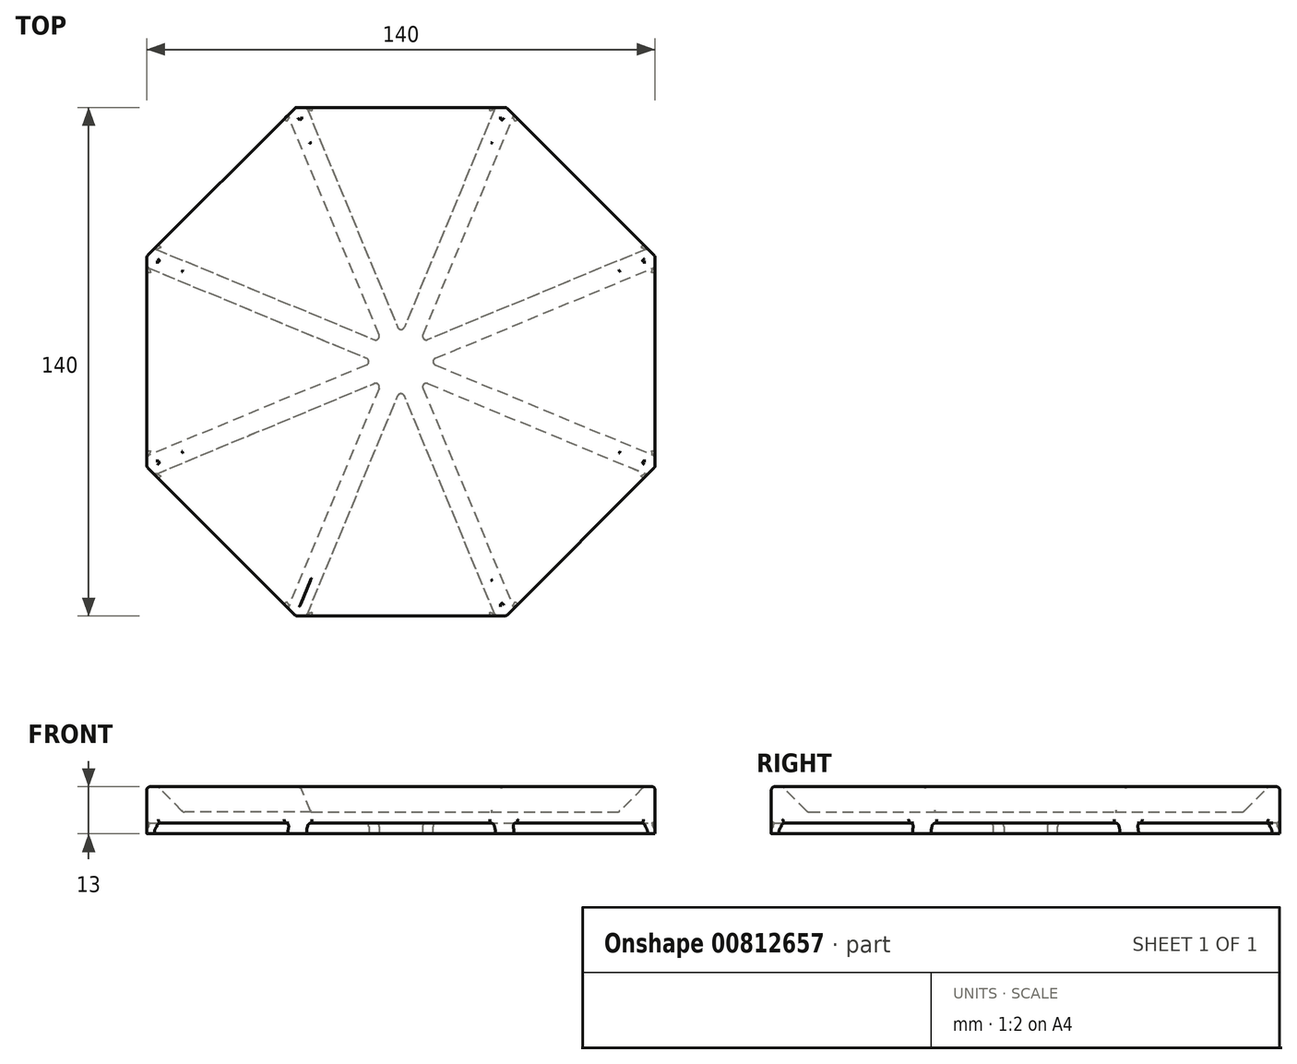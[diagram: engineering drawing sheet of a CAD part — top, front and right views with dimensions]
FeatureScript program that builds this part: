
annotation { "Feature Type Name" : "Feature", "Feature Type Description" : "" }
export const myFeature = defineFeature(function(context is Context, id is Id, definition is map)
    precondition{}
    {
        {
            var Q0;
            Q0=qCreatedBy(makeId("Top.planeOp"),FACE);
            var sketch = newSketch(context, id + "F0", { "sketchPlane" : qUnion([Q0])});
            skCircle(sketch, "E0.cCircle", {"center": v(0, 0) * mm, "radius": 70 * mm, "construction": true});
            skLineSegment(sketch, "E0.0", {"start": v(29, -70) * mm, "end": v(-29, -70) * mm});
            skLineSegment(sketch, "E0.1", {"start": v(-29, -70) * mm, "end": v(-70, -29) * mm});
            skLineSegment(sketch, "E0.2", {"start": v(-70, -29) * mm, "end": v(-70, 29) * mm});
            skLineSegment(sketch, "E0.3", {"start": v(-70, 29) * mm, "end": v(-29, 70) * mm});
            skLineSegment(sketch, "E0.4", {"start": v(-29, 70) * mm, "end": v(29, 70) * mm});
            skLineSegment(sketch, "E0.5", {"start": v(29, 70) * mm, "end": v(70, 29) * mm});
            skLineSegment(sketch, "E0.6", {"start": v(70, 29) * mm, "end": v(70, -29) * mm});
            skLineSegment(sketch, "E0.7", {"start": v(70, -29) * mm, "end": v(29, -70) * mm});
            skPoint(sketch, "E0.0.midPoint", {"position": v(0, -70) * mm});
            skSolve(sketch);
        }
        {
            var Q0;
            Q0 = qSketchRegion(id + "F0", true);
            extrude(context, id + "F1", {"entities" : qUnion([Q0]), "depth" : 10 * mm, "offsetDistance" : 25 * mm});
        }
        {
            var Q0;
            Q0=makeQuery(id+"F1.opExtrude","CAP_FACE",FACE,{"disambiguationData":[OSD([sQuery(id+"F0.wireOp",EDGE,"E0.0"),sQuery(id+"F0.wireOp",EDGE,"E0.1"),sQuery(id+"F0.wireOp",EDGE,"E0.2"),sQuery(id+"F0.wireOp",EDGE,"E0.3"),sQuery(id+"F0.wireOp",EDGE,"E0.4"),sQuery(id+"F0.wireOp",EDGE,"E0.5"),sQuery(id+"F0.wireOp",EDGE,"E0.6"),sQuery(id+"F0.wireOp",EDGE,"E0.7")])],"isStart":false});
            shell(context, id + "F2", {"entities" : qUnion([Q0]), "thickness" : 3 * mm});
        }
        {
            var Q0;
            Q0=makeQuery(id+"F2.opShell","OFFSET_FACE",FACE,{"disambiguationData":[OSD([sQuery(id+"F0.wireOp",EDGE,"E0.0"),sQuery(id+"F0.wireOp",EDGE,"E0.1"),sQuery(id+"F0.wireOp",EDGE,"E0.2"),sQuery(id+"F0.wireOp",EDGE,"E0.3"),sQuery(id+"F0.wireOp",EDGE,"E0.4"),sQuery(id+"F0.wireOp",EDGE,"E0.5"),sQuery(id+"F0.wireOp",EDGE,"E0.6"),sQuery(id+"F0.wireOp",EDGE,"E0.7")])]});
            chamfer(context, id + "F3", {"entities" : qUnion([Q0]), "width" : 7 * mm, "tangentPropagation" : true});
        }
        {
            var Q0;
            Q0=makeQuery(id+"F1.opExtrude","CAP_FACE",FACE,{"disambiguationData":[OSD([sQuery(id+"F0.wireOp",EDGE,"E0.0"),sQuery(id+"F0.wireOp",EDGE,"E0.1"),sQuery(id+"F0.wireOp",EDGE,"E0.2"),sQuery(id+"F0.wireOp",EDGE,"E0.3"),sQuery(id+"F0.wireOp",EDGE,"E0.4"),sQuery(id+"F0.wireOp",EDGE,"E0.5"),sQuery(id+"F0.wireOp",EDGE,"E0.6"),sQuery(id+"F0.wireOp",EDGE,"E0.7")])],"isStart":true});
            var sketch = newSketch(context, id + "F4", { "sketchPlane" : qUnion([Q0])});
            skLineSegment(sketch, "E1", {"start": v(-26, 70) * mm, "end": v(0, 7.24) * mm});
            skLineSegment(sketch, "E2", {"start": v(26, -70) * mm, "end": v(0, -7.24) * mm});
            skLineSegment(sketch, "E3", {"start": v(26, 70) * mm, "end": v(0, 7.24) * mm});
            skLineSegment(sketch, "E4", {"start": v(-26, -70) * mm, "end": v(0, -7.24) * mm});
            skLineSegment(sketch, "E5", {"start": v(-67.88, 31.12) * mm, "end": v(-5.12, 5.12) * mm});
            skLineSegment(sketch, "E6", {"start": v(67.88, -31.12) * mm, "end": v(5.12, -5.12) * mm});
            skLineSegment(sketch, "E7", {"start": v(-70, -26) * mm, "end": v(-7.24, 0) * mm});
            skLineSegment(sketch, "E8", {"start": v(-67.88, -31.12) * mm, "end": v(-5.12, -5.12) * mm});
            skLineSegment(sketch, "E9.trimOffspring", {"start": v(5.12, 5.12) * mm, "end": v(67.88, 31.12) * mm});
            skLineSegment(sketch, "E10.trimOffspring", {"start": v(5.12, 5.12) * mm, "end": v(31.12, 67.88) * mm});
            skLineSegment(sketch, "E11.trimOffspring", {"start": v(7.24, 0) * mm, "end": v(70, -26) * mm});
            skLineSegment(sketch, "E12.trimOffspring", {"start": v(7.24, 0) * mm, "end": v(70, 26) * mm});
            skLineSegment(sketch, "E13.trimOffspring", {"start": v(5.12, -5.12) * mm, "end": v(31.12, -67.88) * mm});
            skLineSegment(sketch, "E14.trimOffspring", {"start": v(-5.12, -5.12) * mm, "end": v(-31.12, -67.88) * mm});
            skLineSegment(sketch, "E15.trimOffspring", {"start": v(-7.24, 0) * mm, "end": v(-70, 26) * mm});
            skLineSegment(sketch, "E16.trimOffspring", {"start": v(-5.12, 5.12) * mm, "end": v(-31.12, 67.88) * mm});
            skSolve(sketch);
        }
        {
            var Q0;
            {var subQ8=sQuery(id+"F4.wireOp",EDGE,"E1");Q0=makeQuery(id+"F4.imprint","IMPRINT",FACE,{"disambiguationData":[TD([[makeQuery(id+"F4.imprint","IMPRINT",EDGE,{"derivedFrom":subQ8}),-1.0]])]});}
            extrude(context, id + "F5", {"entities" : qUnion([Q0]), "operationType" : NewBodyOperationType.ADD, "depth" : 3 * mm, "offsetDistance" : 25 * mm});
        }
        {
            var Q0;
            {var subQ0=sQuery(id+"F0.wireOp",EDGE,"E0.7");var subQ1=sQuery(id+"F0.wireOp",EDGE,"E0.0");var subQ5=sQuery(id+"F0.wireOp",EDGE,"E0.1");Q0=makeQuery(id+"F5.boolean.opBoolean","SPLIT",FACE,{"disambiguationData":[TD([makeQuery(id+"F1.opExtrude","SWEPT_FACE",FACE,{"disambiguationData":[OSD([subQ1])]})])],"derivedFrom":makeQuery(id+"F1.opExtrude","CAP_FACE",FACE,{"disambiguationData":[OSD([subQ1,subQ5,sQuery(id+"F0.wireOp",EDGE,"E0.2"),sQuery(id+"F0.wireOp",EDGE,"E0.3"),sQuery(id+"F0.wireOp",EDGE,"E0.4"),sQuery(id+"F0.wireOp",EDGE,"E0.5"),sQuery(id+"F0.wireOp",EDGE,"E0.6"),subQ0])],"isStart":true})});}
            var Q1;
            {var subQ0=sQuery(id+"F0.wireOp",EDGE,"E0.7");var subQ2=sQuery(id+"F0.wireOp",EDGE,"E0.0");var subQ5=sQuery(id+"F0.wireOp",EDGE,"E0.6");Q1=makeQuery(id+"F5.boolean.opBoolean","SPLIT",FACE,{"disambiguationData":[TD([makeQuery(id+"F1.opExtrude","SWEPT_FACE",FACE,{"disambiguationData":[OSD([subQ0])]})])],"derivedFrom":makeQuery(id+"F1.opExtrude","CAP_FACE",FACE,{"disambiguationData":[OSD([subQ2,sQuery(id+"F0.wireOp",EDGE,"E0.1"),sQuery(id+"F0.wireOp",EDGE,"E0.2"),sQuery(id+"F0.wireOp",EDGE,"E0.3"),sQuery(id+"F0.wireOp",EDGE,"E0.4"),sQuery(id+"F0.wireOp",EDGE,"E0.5"),subQ5,subQ0])],"isStart":true})});}
            var Q2;
            {var subQ0=sQuery(id+"F0.wireOp",EDGE,"E0.6");var subQ2=sQuery(id+"F0.wireOp",EDGE,"E0.5");var subQ5=sQuery(id+"F0.wireOp",EDGE,"E0.7");Q2=makeQuery(id+"F5.boolean.opBoolean","SPLIT",FACE,{"disambiguationData":[TD([makeQuery(id+"F1.opExtrude","SWEPT_FACE",FACE,{"disambiguationData":[OSD([subQ0])]})])],"derivedFrom":makeQuery(id+"F1.opExtrude","CAP_FACE",FACE,{"disambiguationData":[OSD([sQuery(id+"F0.wireOp",EDGE,"E0.0"),sQuery(id+"F0.wireOp",EDGE,"E0.1"),sQuery(id+"F0.wireOp",EDGE,"E0.2"),sQuery(id+"F0.wireOp",EDGE,"E0.3"),sQuery(id+"F0.wireOp",EDGE,"E0.4"),subQ2,subQ0,subQ5])],"isStart":true})});}
            var Q3;
            {var subQ0=sQuery(id+"F0.wireOp",EDGE,"E0.5");var subQ2=sQuery(id+"F0.wireOp",EDGE,"E0.4");var subQ5=sQuery(id+"F0.wireOp",EDGE,"E0.6");Q3=makeQuery(id+"F5.boolean.opBoolean","SPLIT",FACE,{"disambiguationData":[TD([makeQuery(id+"F1.opExtrude","SWEPT_FACE",FACE,{"disambiguationData":[OSD([subQ0])]})])],"derivedFrom":makeQuery(id+"F1.opExtrude","CAP_FACE",FACE,{"disambiguationData":[OSD([sQuery(id+"F0.wireOp",EDGE,"E0.0"),sQuery(id+"F0.wireOp",EDGE,"E0.1"),sQuery(id+"F0.wireOp",EDGE,"E0.2"),sQuery(id+"F0.wireOp",EDGE,"E0.3"),subQ2,subQ0,subQ5,sQuery(id+"F0.wireOp",EDGE,"E0.7")])],"isStart":true})});}
            var Q4;
            {var subQ1=sQuery(id+"F0.wireOp",EDGE,"E0.5");var subQ2=sQuery(id+"F0.wireOp",EDGE,"E0.4");var subQ5=sQuery(id+"F0.wireOp",EDGE,"E0.3");Q4=makeQuery(id+"F5.boolean.opBoolean","SPLIT",FACE,{"disambiguationData":[TD([makeQuery(id+"F1.opExtrude","SWEPT_FACE",FACE,{"disambiguationData":[OSD([subQ2])]})])],"derivedFrom":makeQuery(id+"F1.opExtrude","CAP_FACE",FACE,{"disambiguationData":[OSD([sQuery(id+"F0.wireOp",EDGE,"E0.0"),sQuery(id+"F0.wireOp",EDGE,"E0.1"),sQuery(id+"F0.wireOp",EDGE,"E0.2"),subQ5,subQ2,subQ1,sQuery(id+"F0.wireOp",EDGE,"E0.6"),sQuery(id+"F0.wireOp",EDGE,"E0.7")])],"isStart":true})});}
            var Q5;
            {var subQ0=sQuery(id+"F0.wireOp",EDGE,"E0.3");var subQ2=sQuery(id+"F0.wireOp",EDGE,"E0.2");var subQ5=sQuery(id+"F0.wireOp",EDGE,"E0.4");Q5=makeQuery(id+"F5.boolean.opBoolean","SPLIT",FACE,{"disambiguationData":[TD([makeQuery(id+"F1.opExtrude","SWEPT_FACE",FACE,{"disambiguationData":[OSD([subQ0])]})])],"derivedFrom":makeQuery(id+"F1.opExtrude","CAP_FACE",FACE,{"disambiguationData":[OSD([sQuery(id+"F0.wireOp",EDGE,"E0.0"),sQuery(id+"F0.wireOp",EDGE,"E0.1"),subQ2,subQ0,subQ5,sQuery(id+"F0.wireOp",EDGE,"E0.5"),sQuery(id+"F0.wireOp",EDGE,"E0.6"),sQuery(id+"F0.wireOp",EDGE,"E0.7")])],"isStart":true})});}
            var Q6;
            {var subQ0=sQuery(id+"F0.wireOp",EDGE,"E0.2");var subQ2=sQuery(id+"F0.wireOp",EDGE,"E0.1");var subQ5=sQuery(id+"F0.wireOp",EDGE,"E0.3");Q6=makeQuery(id+"F5.boolean.opBoolean","SPLIT",FACE,{"disambiguationData":[TD([makeQuery(id+"F1.opExtrude","SWEPT_FACE",FACE,{"disambiguationData":[OSD([subQ0])]})])],"derivedFrom":makeQuery(id+"F1.opExtrude","CAP_FACE",FACE,{"disambiguationData":[OSD([sQuery(id+"F0.wireOp",EDGE,"E0.0"),subQ2,subQ0,subQ5,sQuery(id+"F0.wireOp",EDGE,"E0.4"),sQuery(id+"F0.wireOp",EDGE,"E0.5"),sQuery(id+"F0.wireOp",EDGE,"E0.6"),sQuery(id+"F0.wireOp",EDGE,"E0.7")])],"isStart":true})});}
            var Q7;
            {var subQ0=sQuery(id+"F0.wireOp",EDGE,"E0.1");var subQ2=sQuery(id+"F0.wireOp",EDGE,"E0.0");var subQ5=sQuery(id+"F0.wireOp",EDGE,"E0.2");Q7=makeQuery(id+"F5.boolean.opBoolean","SPLIT",FACE,{"disambiguationData":[TD([makeQuery(id+"F1.opExtrude","SWEPT_FACE",FACE,{"disambiguationData":[OSD([subQ0])]})])],"derivedFrom":makeQuery(id+"F1.opExtrude","CAP_FACE",FACE,{"disambiguationData":[OSD([subQ2,subQ0,subQ5,sQuery(id+"F0.wireOp",EDGE,"E0.3"),sQuery(id+"F0.wireOp",EDGE,"E0.4"),sQuery(id+"F0.wireOp",EDGE,"E0.5"),sQuery(id+"F0.wireOp",EDGE,"E0.6"),sQuery(id+"F0.wireOp",EDGE,"E0.7")])],"isStart":true})});}
            var Q8;
            Q8=makeQuery(id+"F5.opExtrude","SWEPT_EDGE",EDGE,{"disambiguationData":[OSD([sQuery(id+"F4.wireOp",EDGE,"E1"),sQuery(id+"F4.wireOp",EDGE,"E3")])]});
            var Q9;
            Q9=makeQuery(id+"F5.opExtrude","SWEPT_EDGE",EDGE,{"disambiguationData":[OSD([sQuery(id+"F4.wireOp",EDGE,"E9.trimOffspring"),sQuery(id+"F4.wireOp",EDGE,"E10.trimOffspring")])]});
            var Q10;
            Q10=makeQuery(id+"F5.opExtrude","SWEPT_EDGE",EDGE,{"disambiguationData":[OSD([sQuery(id+"F4.wireOp",EDGE,"E11.trimOffspring"),sQuery(id+"F4.wireOp",EDGE,"E12.trimOffspring")])]});
            var Q11;
            Q11=makeQuery(id+"F5.opExtrude","SWEPT_EDGE",EDGE,{"disambiguationData":[OSD([sQuery(id+"F4.wireOp",EDGE,"E6"),sQuery(id+"F4.wireOp",EDGE,"E13.trimOffspring")])]});
            var Q12;
            Q12=makeQuery(id+"F5.opExtrude","SWEPT_EDGE",EDGE,{"disambiguationData":[OSD([sQuery(id+"F4.wireOp",EDGE,"E2"),sQuery(id+"F4.wireOp",EDGE,"E4")])]});
            var Q13;
            Q13=makeQuery(id+"F5.opExtrude","SWEPT_EDGE",EDGE,{"disambiguationData":[OSD([sQuery(id+"F4.wireOp",EDGE,"E8"),sQuery(id+"F4.wireOp",EDGE,"E14.trimOffspring")])]});
            var Q14;
            Q14=makeQuery(id+"F5.opExtrude","SWEPT_EDGE",EDGE,{"disambiguationData":[OSD([sQuery(id+"F4.wireOp",EDGE,"E7"),sQuery(id+"F4.wireOp",EDGE,"E15.trimOffspring")])]});
            var Q15;
            Q15=makeQuery(id+"F5.opExtrude","SWEPT_EDGE",EDGE,{"disambiguationData":[OSD([sQuery(id+"F4.wireOp",EDGE,"E5"),sQuery(id+"F4.wireOp",EDGE,"E16.trimOffspring")])]});
            var Q16;
            Q16=makeQuery(id+"F2.opShell","OFFSET_FACE",FACE,{"disambiguationData":[OSD([sQuery(id+"F0.wireOp",EDGE,"E0.0"),sQuery(id+"F0.wireOp",EDGE,"E0.1"),sQuery(id+"F0.wireOp",EDGE,"E0.2"),sQuery(id+"F0.wireOp",EDGE,"E0.3"),sQuery(id+"F0.wireOp",EDGE,"E0.4"),sQuery(id+"F0.wireOp",EDGE,"E0.5"),sQuery(id+"F0.wireOp",EDGE,"E0.6"),sQuery(id+"F0.wireOp",EDGE,"E0.7")])]});
            var Q17;
            {var subQ0=sQuery(id+"F0.wireOp",EDGE,"E0.3");var subQ1=sQuery(id+"F0.wireOp",EDGE,"E0.2");Q17=makeQuery(id+"F3.opChamfer","BLEND_EDGE",EDGE,{"blendedFrom":[makeQuery(id+"F2.opShell","OFFSET_EDGE",EDGE,{"disambiguationData":[OSD([subQ1]),TDD([makeQuery(id+"F1.opExtrude","CAP_EDGE",EDGE,{"disambiguationData":[OSD([subQ1])],"isStart":true})])]}),makeQuery(id+"F2.opShell","OFFSET_EDGE",EDGE,{"disambiguationData":[OSD([subQ0]),TDD([makeQuery(id+"F1.opExtrude","CAP_EDGE",EDGE,{"disambiguationData":[OSD([subQ0])],"isStart":true})])]})],"blendedInto":[]});}
            var Q18;
            {var subQ0=sQuery(id+"F0.wireOp",EDGE,"E0.4");var subQ1=sQuery(id+"F0.wireOp",EDGE,"E0.3");Q18=makeQuery(id+"F3.opChamfer","BLEND_EDGE",EDGE,{"blendedFrom":[makeQuery(id+"F2.opShell","OFFSET_EDGE",EDGE,{"disambiguationData":[OSD([subQ1]),TDD([makeQuery(id+"F1.opExtrude","CAP_EDGE",EDGE,{"disambiguationData":[OSD([subQ1])],"isStart":true})])]}),makeQuery(id+"F2.opShell","OFFSET_EDGE",EDGE,{"disambiguationData":[OSD([subQ0]),TDD([makeQuery(id+"F1.opExtrude","CAP_EDGE",EDGE,{"disambiguationData":[OSD([subQ0])],"isStart":true})])]})],"blendedInto":[]});}
            var Q19;
            {var subQ0=sQuery(id+"F0.wireOp",EDGE,"E0.5");var subQ1=sQuery(id+"F0.wireOp",EDGE,"E0.4");Q19=makeQuery(id+"F3.opChamfer","BLEND_EDGE",EDGE,{"blendedFrom":[makeQuery(id+"F2.opShell","OFFSET_EDGE",EDGE,{"disambiguationData":[OSD([subQ1]),TDD([makeQuery(id+"F1.opExtrude","CAP_EDGE",EDGE,{"disambiguationData":[OSD([subQ1])],"isStart":true})])]}),makeQuery(id+"F2.opShell","OFFSET_EDGE",EDGE,{"disambiguationData":[OSD([subQ0]),TDD([makeQuery(id+"F1.opExtrude","CAP_EDGE",EDGE,{"disambiguationData":[OSD([subQ0])],"isStart":true})])]})],"blendedInto":[]});}
            var Q20;
            {var subQ0=sQuery(id+"F0.wireOp",EDGE,"E0.6");var subQ1=sQuery(id+"F0.wireOp",EDGE,"E0.5");Q20=makeQuery(id+"F3.opChamfer","BLEND_EDGE",EDGE,{"blendedFrom":[makeQuery(id+"F2.opShell","OFFSET_EDGE",EDGE,{"disambiguationData":[OSD([subQ1]),TDD([makeQuery(id+"F1.opExtrude","CAP_EDGE",EDGE,{"disambiguationData":[OSD([subQ1])],"isStart":true})])]}),makeQuery(id+"F2.opShell","OFFSET_EDGE",EDGE,{"disambiguationData":[OSD([subQ0]),TDD([makeQuery(id+"F1.opExtrude","CAP_EDGE",EDGE,{"disambiguationData":[OSD([subQ0])],"isStart":true})])]})],"blendedInto":[]});}
            var Q21;
            {var subQ0=sQuery(id+"F0.wireOp",EDGE,"E0.7");var subQ1=sQuery(id+"F0.wireOp",EDGE,"E0.6");Q21=makeQuery(id+"F3.opChamfer","BLEND_EDGE",EDGE,{"blendedFrom":[makeQuery(id+"F2.opShell","OFFSET_EDGE",EDGE,{"disambiguationData":[OSD([subQ1]),TDD([makeQuery(id+"F1.opExtrude","CAP_EDGE",EDGE,{"disambiguationData":[OSD([subQ1])],"isStart":true})])]}),makeQuery(id+"F2.opShell","OFFSET_EDGE",EDGE,{"disambiguationData":[OSD([subQ0]),TDD([makeQuery(id+"F1.opExtrude","CAP_EDGE",EDGE,{"disambiguationData":[OSD([subQ0])],"isStart":true})])]})],"blendedInto":[]});}
            var Q22;
            {var subQ0=sQuery(id+"F0.wireOp",EDGE,"E0.7");var subQ1=sQuery(id+"F0.wireOp",EDGE,"E0.0");Q22=makeQuery(id+"F3.opChamfer","BLEND_EDGE",EDGE,{"blendedFrom":[makeQuery(id+"F2.opShell","OFFSET_EDGE",EDGE,{"disambiguationData":[OSD([subQ1]),TDD([makeQuery(id+"F1.opExtrude","CAP_EDGE",EDGE,{"disambiguationData":[OSD([subQ1])],"isStart":true})])]}),makeQuery(id+"F2.opShell","OFFSET_EDGE",EDGE,{"disambiguationData":[OSD([subQ0]),TDD([makeQuery(id+"F1.opExtrude","CAP_EDGE",EDGE,{"disambiguationData":[OSD([subQ0])],"isStart":true})])]})],"blendedInto":[]});}
            var Q23;
            {var subQ0=sQuery(id+"F0.wireOp",EDGE,"E0.2");var subQ1=sQuery(id+"F0.wireOp",EDGE,"E0.1");Q23=makeQuery(id+"F3.opChamfer","BLEND_EDGE",EDGE,{"blendedFrom":[makeQuery(id+"F2.opShell","OFFSET_EDGE",EDGE,{"disambiguationData":[OSD([subQ1]),TDD([makeQuery(id+"F1.opExtrude","CAP_EDGE",EDGE,{"disambiguationData":[OSD([subQ1])],"isStart":true})])]}),makeQuery(id+"F2.opShell","OFFSET_EDGE",EDGE,{"disambiguationData":[OSD([subQ0]),TDD([makeQuery(id+"F1.opExtrude","CAP_EDGE",EDGE,{"disambiguationData":[OSD([subQ0])],"isStart":true})])]})],"blendedInto":[]});}
            var Q24;
            Q24=makeQuery(id+"F1.opExtrude","CAP_FACE",FACE,{"disambiguationData":[OSD([sQuery(id+"F0.wireOp",EDGE,"E0.0"),sQuery(id+"F0.wireOp",EDGE,"E0.1"),sQuery(id+"F0.wireOp",EDGE,"E0.2"),sQuery(id+"F0.wireOp",EDGE,"E0.3"),sQuery(id+"F0.wireOp",EDGE,"E0.4"),sQuery(id+"F0.wireOp",EDGE,"E0.5"),sQuery(id+"F0.wireOp",EDGE,"E0.6"),sQuery(id+"F0.wireOp",EDGE,"E0.7")])],"isStart":false});
            var Q25;
            {var subQ0=sQuery(id+"F0.wireOp",EDGE,"E0.2");var subQ1=sQuery(id+"F0.wireOp",EDGE,"E0.1");Q25=makeQuery(id+"F5.boolean.opBoolean","MERGE",EDGE,{"derivedFrom":[makeQuery(id+"F1.opExtrude","SWEPT_EDGE",EDGE,{"disambiguationData":[OSD([subQ1,subQ0])]}),makeQuery(id+"F5.opExtrude","SWEPT_EDGE",EDGE,{"disambiguationData":[OSD([subQ1,subQ0])]})]});}
            var Q26;
            {var subQ0=sQuery(id+"F0.wireOp",EDGE,"E0.3");var subQ1=sQuery(id+"F0.wireOp",EDGE,"E0.2");Q26=makeQuery(id+"F5.boolean.opBoolean","MERGE",EDGE,{"derivedFrom":[makeQuery(id+"F1.opExtrude","SWEPT_EDGE",EDGE,{"disambiguationData":[OSD([subQ1,subQ0])]}),makeQuery(id+"F5.opExtrude","SWEPT_EDGE",EDGE,{"disambiguationData":[OSD([subQ1,subQ0])]})]});}
            var Q27;
            {var subQ0=sQuery(id+"F0.wireOp",EDGE,"E0.4");var subQ1=sQuery(id+"F0.wireOp",EDGE,"E0.3");Q27=makeQuery(id+"F5.boolean.opBoolean","MERGE",EDGE,{"derivedFrom":[makeQuery(id+"F1.opExtrude","SWEPT_EDGE",EDGE,{"disambiguationData":[OSD([subQ1,subQ0])]}),makeQuery(id+"F5.opExtrude","SWEPT_EDGE",EDGE,{"disambiguationData":[OSD([subQ1,subQ0])]})]});}
            var Q28;
            {var subQ0=sQuery(id+"F0.wireOp",EDGE,"E0.5");var subQ1=sQuery(id+"F0.wireOp",EDGE,"E0.4");Q28=makeQuery(id+"F5.boolean.opBoolean","MERGE",EDGE,{"derivedFrom":[makeQuery(id+"F1.opExtrude","SWEPT_EDGE",EDGE,{"disambiguationData":[OSD([subQ1,subQ0])]}),makeQuery(id+"F5.opExtrude","SWEPT_EDGE",EDGE,{"disambiguationData":[OSD([subQ1,subQ0])]})]});}
            var Q29;
            {var subQ0=sQuery(id+"F0.wireOp",EDGE,"E0.6");var subQ1=sQuery(id+"F0.wireOp",EDGE,"E0.5");Q29=makeQuery(id+"F5.boolean.opBoolean","MERGE",EDGE,{"derivedFrom":[makeQuery(id+"F1.opExtrude","SWEPT_EDGE",EDGE,{"disambiguationData":[OSD([subQ1,subQ0])]}),makeQuery(id+"F5.opExtrude","SWEPT_EDGE",EDGE,{"disambiguationData":[OSD([subQ1,subQ0])]})]});}
            var Q30;
            {var subQ0=sQuery(id+"F0.wireOp",EDGE,"E0.7");var subQ1=sQuery(id+"F0.wireOp",EDGE,"E0.6");Q30=makeQuery(id+"F5.boolean.opBoolean","MERGE",EDGE,{"derivedFrom":[makeQuery(id+"F1.opExtrude","SWEPT_EDGE",EDGE,{"disambiguationData":[OSD([subQ1,subQ0])]}),makeQuery(id+"F5.opExtrude","SWEPT_EDGE",EDGE,{"disambiguationData":[OSD([subQ1,subQ0])]})]});}
            var Q31;
            {var subQ0=sQuery(id+"F0.wireOp",EDGE,"E0.7");var subQ1=sQuery(id+"F0.wireOp",EDGE,"E0.0");Q31=makeQuery(id+"F5.boolean.opBoolean","MERGE",EDGE,{"derivedFrom":[makeQuery(id+"F1.opExtrude","SWEPT_EDGE",EDGE,{"disambiguationData":[OSD([subQ1,subQ0])]}),makeQuery(id+"F5.opExtrude","SWEPT_EDGE",EDGE,{"disambiguationData":[OSD([subQ1,subQ0])]})]});}
            var Q32;
            {var subQ0=sQuery(id+"F0.wireOp",EDGE,"E0.1");var subQ1=sQuery(id+"F0.wireOp",EDGE,"E0.0");Q32=makeQuery(id+"F5.boolean.opBoolean","MERGE",EDGE,{"derivedFrom":[makeQuery(id+"F1.opExtrude","SWEPT_EDGE",EDGE,{"disambiguationData":[OSD([subQ1,subQ0])]}),makeQuery(id+"F5.opExtrude","SWEPT_EDGE",EDGE,{"disambiguationData":[OSD([subQ1,subQ0])]})]});}
            fillet(context, id + "F6", {"entities" : qUnion([Q0, Q1, Q2, Q3, Q4, Q5, Q6, Q7, Q8, Q9, Q10, Q11, Q12, Q13, Q14, Q15, Q16, Q17, Q18, Q19, Q20, Q21, Q22, Q23, Q24, Q25, Q26, Q27, Q28, Q29, Q30, Q31, Q32]), "radius" : 1 * mm, "tangentPropagation" : true, "allowEdgeOverflow" : false});
        }
    });
